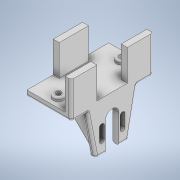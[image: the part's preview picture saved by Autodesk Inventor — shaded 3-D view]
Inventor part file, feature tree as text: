
AUTODESK INVENTOR PART (.ipt)
format: ipt  version: 2020 (Build 240168000, 168)  size: 317,952 bytes
history: native  units: in
note: dims shown in document units (in); Inventor stores cm internally (conversion verified against a paired STEP export)
features: extrude x10, sketch x9, fillet x6
ambient origin geometry x8: Origin, YZ Plane, XZ Plane, XY Plane, X Axis, Y Axis, Z Axis, Center Point
bodies: Solid1 (feature_tree)
feature tree (25):
  extrude  "Extrusion1"  Depth=2.6378in
  extrude  "Extrusion2"  Depth=0.1969in
  extrude  "Extrusion3"  Depth=0.1969in
  extrude  "Extrusion4"  Depth=1.0in TaperAngle=0.0deg
  extrude  "Extrusion5"  Depth=0.3346in
  fillet  "Fillet1"  Radius=0.3346in
  fillet  "Fillet2"  Radius=0.1181in
  extrude  "Extrusion6"  Depth=0.2362in
  extrude  "Extrusion7"  Depth=0.1575in
  extrude  "Extrusion8"  Depth=0.5906in TaperAngle=0.0deg
  fillet  "Fillet10"  Radius=0.0591in
  extrude  "Extrusion11"  Depth=0.1969in
  extrude  "Extrusion12"  Depth=0.0748in
  fillet  "Fillet11"  Radius=1.0in
  fillet  "Fillet12"  Radius=0.7165in
  fillet  "Fillet13"  Radius=0.7165in
  sketch  "Sketch1"  dims[d0=1.4331in d1=2.6378in]
  sketch  "Sketch2"  dims[d2=0.1969in d3=0.0in d4=0.1969in]
  sketch  "Sketch3"  dims[d5=0.8268in d6=0.1969in]
  sketch  "Sketch4"  dims[d7=0.8268in d8=1.0in d9=0.0in]
  sketch  "Sketch6"  dims[d10=0.3346in d11=0.3346in d12=0.3346in d13=0.1181in d14=0.0in]
  sketch  "Sketch7"  dims[d15=0.2362in d16=0.2362in]
  sketch  "Sketch8"  dims[d17=0.1181in d18=0.0in d19=0.1575in]
  sketch  "Sketch11"  dims[d21=0.1575in d22=0.5906in d23=0.0in d24=0.0591in]
  sketch  "Sketch12"  dims[d25=0.0787in d26=0.1969in d27=0.9449in d28=1.0in d29=0.0in d30=0.7165in d31=0.7165in d32=0.1575in d33=1.6142in d34=1.4094in d35=0.1969in d36=0.0in d37=0.0in d38=0.1575in d39=0.1575in d40=0.4331in d42=1.0157in d43=0.0in d47=0.6102in d48=0.6102in d49=0.0591in d50=0.1575in d51=0.1575in d52=0.1575in d53=0.1575in d64=0.2756in d65=0.2756in d66=0.2165in d67=0.1181in d68=0.1181in d69=1.063in d70=0.0in d71=1.5748in d72=0.0in d73=0.0591in d74=0.0748in d75=0.0748in]
